# Revit family: ECOJET-06DIA-LENGTH
name_source: partatom
category: Air Terminals
revit_build: Autodesk Revit 2018 (Build: 20170223_1515(x64)
units: mm (PartAtom-declared; Revit-internal decimal feet)

## family parameters
Always vertical = Yes
Cut with Voids When Loaded = No
Part Type = Normal
Room Calculation Point = No
Round Connector Dimension = Use Diameter
Shared = No
Work Plane-Based = No

## types (7) — shared parameters
ADIM = 0' - 3"
BOXHI = 0' - 7"
ECOJETBOX = ECBOX-06
HIOVER = 0' - 2"
Manufacturer = Anemostat-HVAC
Model = ECOJET DRUM LOUVER
NORHI = 0' - 6"
RADIUS = 0' - 3"
URL = anemostat-hvac.com
WIDOVER = 0' - 2 3/4"

## per-type parameters (varying)
| type | BOXWID | DUCTWID | NORMLENGTH | NORWID |
| ECOJET-18-06D | 1' - 8 11/16" | 1' - 7" | 1' - 6" | 1' - 5 15/16" |
| ECOJET-12-06D | 1' - 2 11/16" | 1' - 1" | 1' - 0" | 0' - 11 15/16" |
| ECOJET-09-06D | 0' - 11 11/16" | 0' - 10" | 0' - 9" | 0' - 8 15/16" |
| ECOJET-24-06D | 2' - 2 11/16" | 2' - 1" | 2' - 0" | 1' - 11 15/16" |
| ECOJET-36-06D | 3' - 2 11/16" | 3' - 1" | 3' - 0" | 2' - 11 15/16" |
| ECOJET-48-06D | 4' - 2 11/16" | 4' - 1" | 4' - 0" | 3' - 11 15/16" |
| ECOJET-60-06D | 5' - 2 11/16" | 5' - 1" | 5' - 0" | 4' - 11 15/16" |

## geometry (parser evidence)
native form markers: Sweep x7
no freeform markers — native parametric forms only
